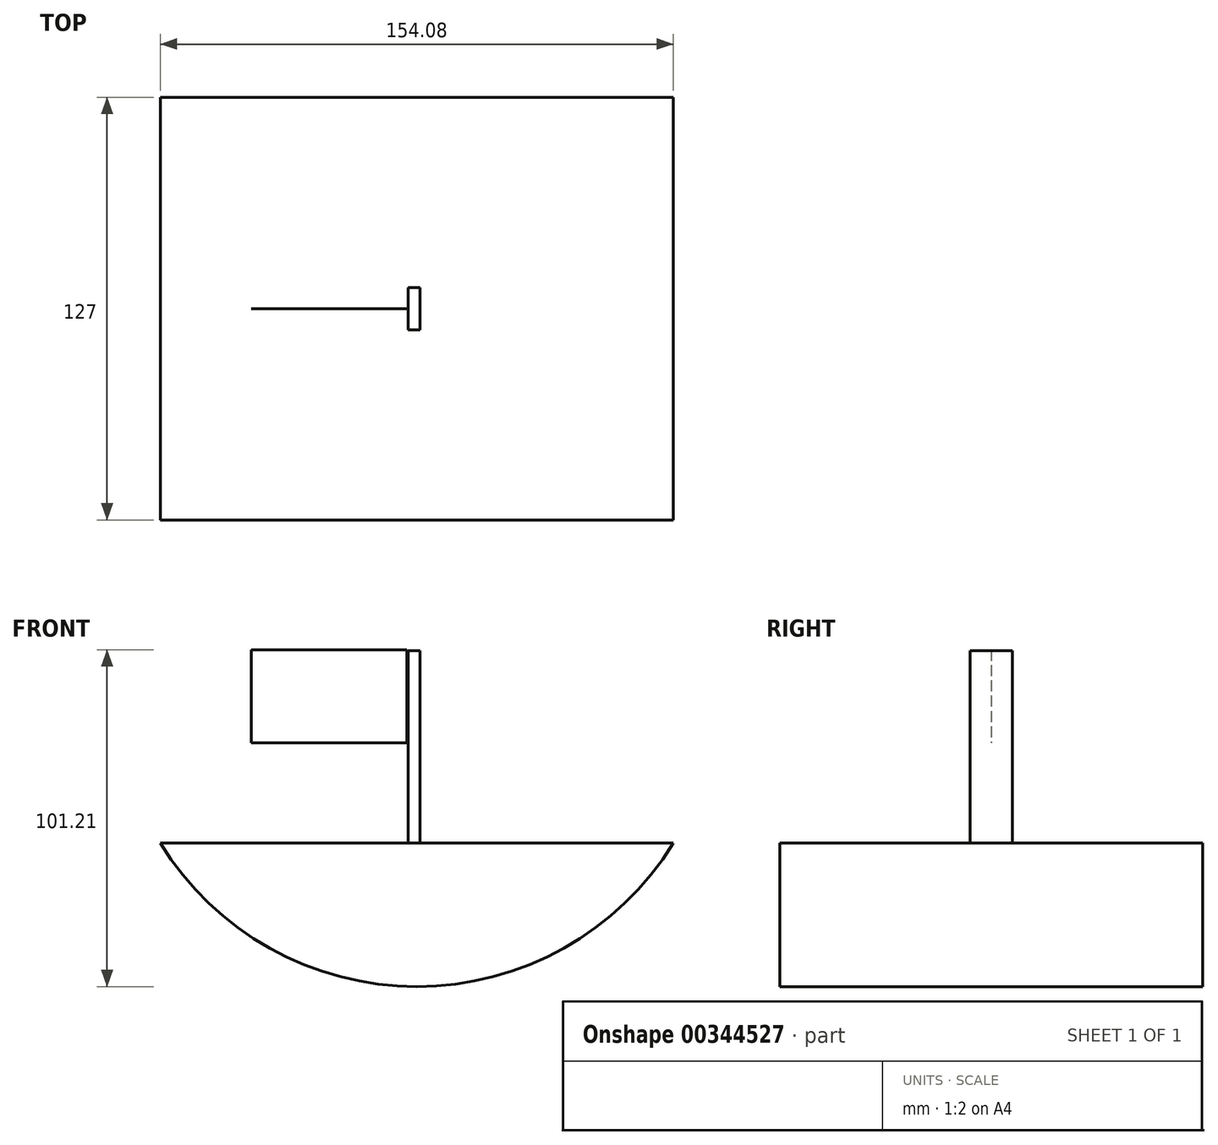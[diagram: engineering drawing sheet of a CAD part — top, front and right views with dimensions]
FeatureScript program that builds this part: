
annotation { "Feature Type Name" : "Feature", "Feature Type Description" : "" }
export const myFeature = defineFeature(function(context is Context, id is Id, definition is map)
    precondition{}
    {
        {
            var Q0;
            Q0=qCreatedBy(makeId("Front.planeOp"),FACE);
            var sketch = newSketch(context, id + "F0", { "sketchPlane" : qUnion([Q0])});
            skLineSegment(sketch, "E0", {"start": v(-78, 0) * mm, "end": v(76.08, 0) * mm});
            skArc(sketch, "E1", {"start": v(-78, 0) * mm, "mid": v(-0.96, -43.08) * mm, "end": v(76.08, 0) * mm});
            skSolve(sketch);
        }
        {
            var Q0;
            Q0=qCreatedBy(makeId("Front.planeOp"),FACE);
            var sketch = newSketch(context, id + "F1", { "sketchPlane" : qUnion([Q0])});
            skLineSegment(sketch, "E2", {"start": v(0, 0) * mm, "end": v(0, 57.83) * mm});
            skLineSegment(sketch, "E3", {"start": v(0, 57.83) * mm, "end": v(-3.6, 57.83) * mm});
            skLineSegment(sketch, "E4", {"start": v(-3.6, 57.83) * mm, "end": v(-3.6, 0) * mm});
            skLineSegment(sketch, "E5", {"start": v(-3.6, 0) * mm, "end": v(0, 0) * mm});
            skSolve(sketch);
        }
        {
            var Q0;
            Q0=qCreatedBy(makeId("Front.planeOp"),FACE);
            var sketch = newSketch(context, id + "F2", { "sketchPlane" : qUnion([Q0])});
            skLineSegment(sketch, "E6.bottom", {"start": v(-3.9, 58.13) * mm, "end": v(-50.66, 58.13) * mm});
            skLineSegment(sketch, "E6.top", {"start": v(-3.9, 30.2) * mm, "end": v(-50.66, 30.2) * mm});
            skLineSegment(sketch, "E6.left", {"start": v(-3.9, 58.13) * mm, "end": v(-3.9, 30.2) * mm});
            skLineSegment(sketch, "E6.right", {"start": v(-50.66, 58.13) * mm, "end": v(-50.66, 30.2) * mm});
            skSolve(sketch);
        }
        {
            var Q0;
            Q0 = qSketchRegion(id + "F0", true);
            extrude(context, id + "F3", {"entities" : qUnion([Q0]), "endBound" : BoundingType.SYMMETRIC, "depth" : 127 * mm});
        }
        {
            var Q0;
            Q0 = qSketchRegion(id + "F2", true);
            extrude(context, id + "F4", {"entities" : qUnion([Q0]), "depth" : 0.03 * mm});
        }
        {
            var Q0;
            Q0 = qSketchRegion(id + "F1", true);
            extrude(context, id + "F5", {"entities" : qUnion([Q0]), "operationType" : NewBodyOperationType.ADD, "endBound" : BoundingType.SYMMETRIC, "depth" : 12.7 * mm});
        }
    });
